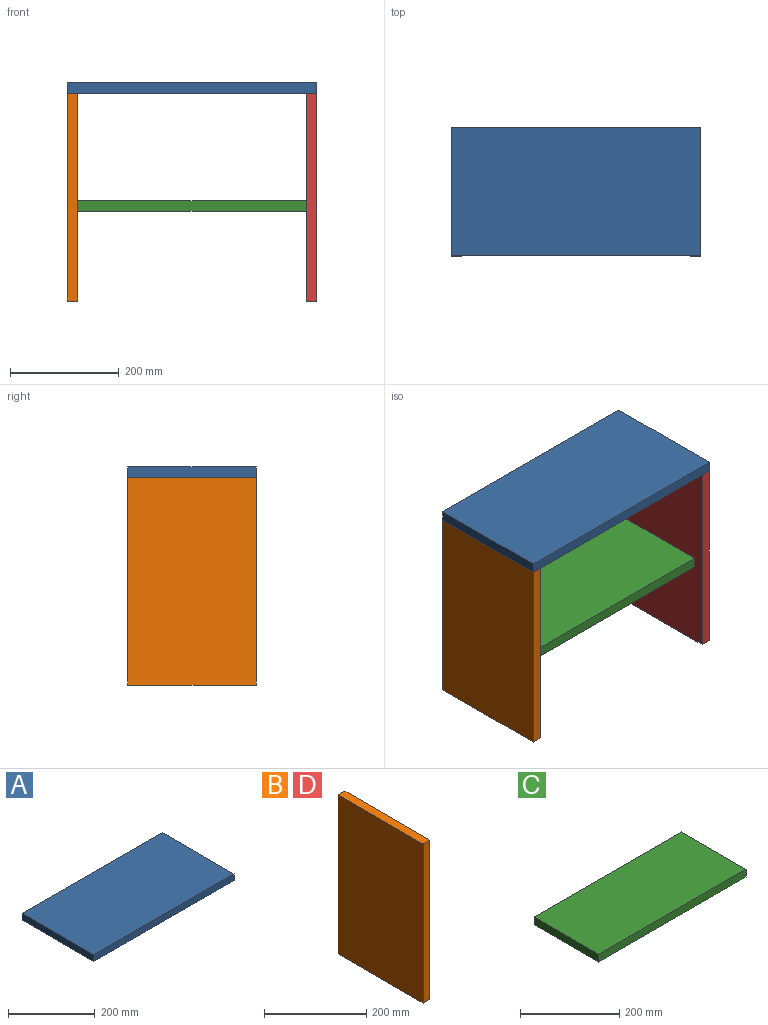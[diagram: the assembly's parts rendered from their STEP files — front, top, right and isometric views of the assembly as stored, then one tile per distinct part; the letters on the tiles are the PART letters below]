
ASSEMBLY  parts=4 mates=3
PART A: 6 faces, bbox 457.2x235x19.1 mm
  f0: plane 234.95x19.05mm, normal (1,0,0), area 4475.8mm2, adj f1,f3,f4,f5
  f1: plane 457.2x19.05mm, normal (0,1,0), area 8709.7mm2, adj f0,f2,f4,f5
  f2: plane 234.95x19.05mm, normal (-1,0,0), area 4475.8mm2, adj f1,f3,f4,f5
  f3: plane 457.2x19.05mm, normal (0,-1,0), area 8709.7mm2, adj f0,f2,f4,f5
  f4: plane 457.2x234.95mm, normal (0,0,1), area 107419.1mm2, adj f0,f1,f2,f3
  f5: plane 457.2x234.95mm, normal (0,0,-1), area 107419.1mm2, adj f0,f1,f2,f3
PART B: 6 faces, bbox 19.1x235x381 mm
  f0: plane 381x19.05mm, normal (0,-1,0), area 7258.1mm2, adj f1,f3,f4,f5
  f1: plane 234.95x19.05mm, normal (0,0,-1), area 4475.8mm2, adj f0,f2,f4,f5
  f2: plane 381x19.05mm, normal (0,1,0), area 7258.1mm2, adj f1,f3,f4,f5
  f3: plane 234.95x19.05mm, normal (0,0,1), area 4475.8mm2, adj f0,f2,f4,f5
  f4: plane 381x234.95mm, normal (1,0,0), area 89515.9mm2, adj f0,f1,f2,f3
  f5: plane 381x234.95mm, normal (-1,0,0), area 89515.9mm2, adj f0,f1,f2,f3
PART C: 6 faces, bbox 419.1x184.2x19.1 mm
  f0: plane 184.15x19.05mm, normal (1,0,0), area 3508.1mm2, adj f1,f3,f4,f5
  f1: plane 419.1x19.05mm, normal (0,1,0), area 7983.9mm2, adj f0,f2,f4,f5
  f2: plane 184.15x19.05mm, normal (-1,0,0), area 3508.1mm2, adj f1,f3,f4,f5
  f3: plane 419.1x19.05mm, normal (0,-1,0), area 7983.9mm2, adj f0,f2,f4,f5
  f4: plane 419.1x184.15mm, normal (0,0,1), area 77177.3mm2, adj f0,f1,f2,f3
  f5: plane 419.1x184.15mm, normal (0,0,-1), area 77177.3mm2, adj f0,f1,f2,f3
PART D: same geometry as B
PLACE A t=(-64.33,-219,268.27)mm
PLACE B t=(-267.53,239.96,-112.73)mm
PLACE C t=(-38.93,13.44,52.37)mm
PLACE D t=(170.62,239.96,-112.73)mm
MATE fastened B.f3 <-> A.f5  axis (0,0,1) through (-267.53,19.79,268.27)mm
MATE fastened B.f4 <-> C.f2  axis (1,0,0) through (-248.48,-78.63,52.37)mm
MATE fastened D.f3 <-> A.f5  axis (0,0,1) through (189.67,19.79,268.27)mm
